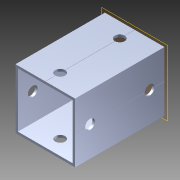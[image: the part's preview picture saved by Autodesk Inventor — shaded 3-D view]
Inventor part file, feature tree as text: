
AUTODESK INVENTOR PART (.ipt)
format: ipt  version: 2014 SP1 (Build 180222100, 222)  size: 1,184,768 bytes
history: native  units: in
note: dims shown in document units (in); Inventor stores cm internally (conversion verified against a paired STEP export)
features: extrude x2, sketch x2, pattern_circular x1, other x1, plane x1, imported_body x1
ambient origin geometry x8: Origin, YZ Plane, XZ Plane, XY Plane, X Axis, Y Axis, Z Axis, Center Point
bodies: Body1 (feature_tree)
feature tree (8):
  pattern_circular  "CirPattern2"
  other  "217-3426-STEP1"
  plane  "Work Plane1"
  extrude  "Extrusion1"  Depth=3937.0079in TaperAngle=0.0deg
  extrude  "Extrusion2"  [1 undecoded]
  imported_body  "Base1"
  sketch  "Sketch1"  dims[d0=-2.25in d1=3937.0079in d2=0.0in]
  sketch  "Sketch3"  dims[d3=0.25in d4=0.0in]
note: 1 required parameter value undecoded (feature->parameter linkage not recoverable at this tier; creation-order binding heuristic only, values carry confidence <= 0.55)
